FCSTD DOCUMENT  (FreeCAD 1.0R39319 (Git))
Label: CharlieSD-layout
License: All rights reserved
LicenseURL: https://en.wikipedia.org/wiki/All_rights_reserved
objects: Sketcher::SketchObject×1, PartDesign::Body×1
note: 3 computed .brp shape members not serialized (recipe doc carries the construction recipe); baked Part::Feature solids carry a one-line shape summary decoded from their .brp

FEATURE [Sketcher::SketchObject] Sketch
  ArcFitTolerance = 1e-06
  AttachmentSupport = -> [XY_Plane]
  FullyConstrained = true
  MakeInternals = false
  MapMode = 5
  sketch-geometry (13):
    g0: LineSegment StartX=70 StartY=24 StartZ=0 EndX=70 EndY=0 EndZ=0
    g1: LineSegment StartX=70 StartY=0 StartZ=0 EndX=11.4 EndY=0 EndZ=0
    g2: LineSegment StartX=11.4 StartY=0 StartZ=0 EndX=11.4 EndY=0.7 EndZ=0
    g3: LineSegment StartX=11.4 StartY=0.7 StartZ=0 EndX=9.7 EndY=0.7 EndZ=0
    g4: LineSegment StartX=9.7 StartY=0.7 StartZ=0 EndX=9.7 EndY=0 EndZ=0
    g5: LineSegment StartX=9.7 StartY=0 StartZ=0 EndX=4 EndY=0 EndZ=0
    g6: LineSegment StartX=4 StartY=0 StartZ=0 EndX=0 EndY=4 EndZ=0
    g7: LineSegment StartX=0 StartY=4 StartZ=0 EndX=0 EndY=24 EndZ=0
    g8: LineSegment StartX=0 StartY=24 StartZ=0 EndX=10.6 EndY=24 EndZ=0
    g9: LineSegment StartX=10.6 StartY=24 StartZ=0 EndX=10.6 EndY=23.3 EndZ=0
    g10: LineSegment StartX=10.6 StartY=23.3 StartZ=0 EndX=14.6 EndY=23.3 EndZ=0
    g11: LineSegment StartX=14.6 StartY=23.3 StartZ=0 EndX=14.6 EndY=24 EndZ=0
    g12: LineSegment StartX=14.6 StartY=24 StartZ=0 EndX=70 EndY=24 EndZ=0
  constraints (39):
    c: PointOnObject(g7,g-2)
    c: PointOnObject(g0,g-1)
    c: Vertical(g0)
    c: Coincident(g1,g0)
    c: PointOnObject(g1,g-1)
    c: Coincident(g2,g1)
    c: Vertical(g2)
    c: Coincident(g3,g2)
    c: Horizontal(g3)
    c: Coincident(g4,g3)
    c: PointOnObject(g4,g-1)
    c: Vertical(g4)
    c: Coincident(g5,g4)
    c: PointOnObject(g5,g-1)
    c: Coincident(g6,g5)
    c: PointOnObject(g6,g-2)
    c: Coincident(g7,g6)
    c: Coincident(g8,g7)
    c: Horizontal(g8)
    c: Coincident(g9,g8)
    c: Vertical(g9)
    c: Coincident(g10,g9)
    c: Horizontal(g10)
    c: Coincident(g11,g10)
    c: Vertical(g11)
    c: Coincident(g12,g11)
    c: Horizontal(g12)
    c: Coincident(g12,g0)
    c: Angle(g6,g-1) = 0.785398
    c: DistanceX(g5,g5) = 5.7
    c: DistanceX(g3,g3) = 1.7
    c: DistanceY(g7,g7) = 20
    c: DistanceY(g2,g2) = 0.7
    c: DistanceY(g0,g0) = 24
    c: DistanceX(g10,g10) = 4
    c: Distance(g7,g9) = 10.6
    c: DistanceY(g9,g9) = 0.7
    c: Equal(g9,g11)
    c: Distance(g0,g7) = 70
FEATURE [PartDesign::Body] Body
  AllowCompound = false
  Group = -> [Sketch]
  Origin = -> Origin
